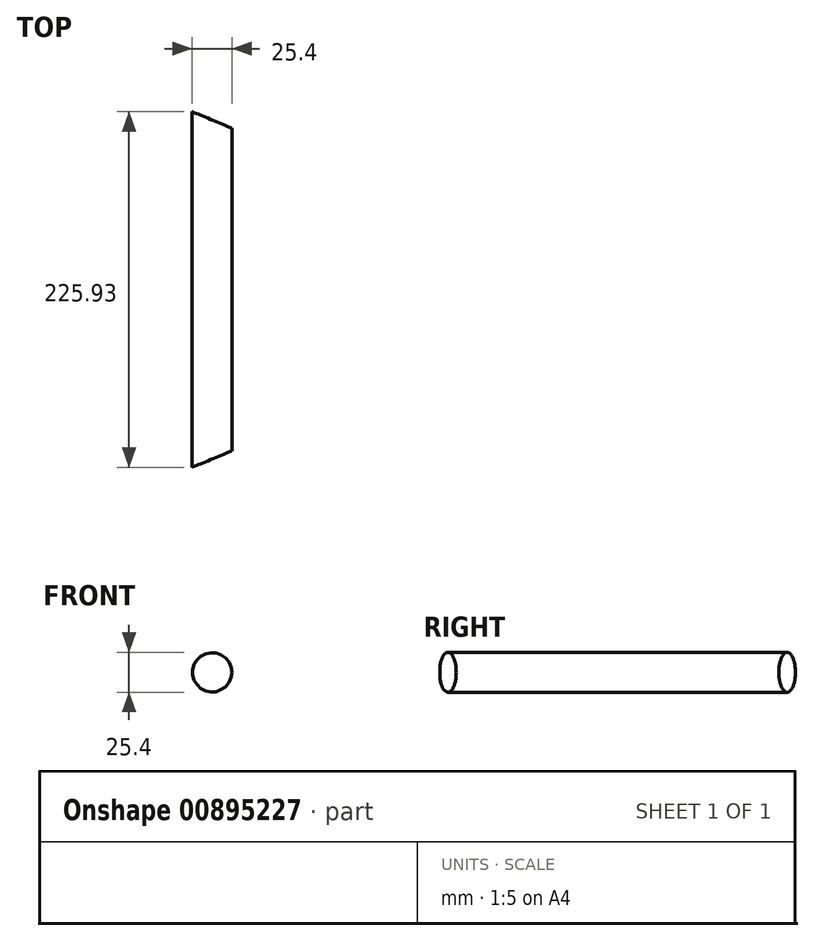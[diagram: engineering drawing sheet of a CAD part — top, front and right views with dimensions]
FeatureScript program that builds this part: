
annotation { "Feature Type Name" : "Feature", "Feature Type Description" : "" }
export const myFeature = defineFeature(function(context is Context, id is Id, definition is map)
    precondition{}
    {
        {
            var Q0;
            Q0=qCreatedBy(makeId("Front.planeOp"),FACE);
            var sketch = newSketch(context, id + "F0", { "sketchPlane" : qUnion([Q0])});
            skCircle(sketch, "E0", {"center": v(0, 0) * mm, "radius": 12.7 * mm});
            skSolve(sketch);
        }
        {
            var Q0;
            Q0=makeQuery(id+"F0.imprint","IMPRINT",FACE,{"disambiguationData":[TD([[makeQuery(id+"F0.imprint","IMPRINT",EDGE,{"derivedFrom":sQuery(id+"F0.wireOp",EDGE,"E0")}),1.0]])]});
            var sketch = newSketch(context, id + "F1", { "sketchPlane" : qUnion([Q0])});
            skSolve(sketch);
        }
        {
            var Q0;
            Q0=qSketchRegion(id+"F1",true);
            var Q1;
            Q1=makeQuery(id+"F1.imprint","IMPRINT",FACE,{"disambiguationData":[TD([[makeQuery(id+"F1.imprint","IMPRINT",EDGE,{"derivedFrom":makeQuery(id+"F0.imprint","IMPRINT",EDGE,{"derivedFrom":sQuery(id+"F0.wireOp",EDGE,"E0")})}),1.0]])]});
            extrude(context, id + "F2", {"entities" : qUnion([Q0, Q1]), "depth" : 225.93 * mm, "offsetDistance" : 25.4 * mm});
        }
        {
            var Q0;
            Q0=makeQuery(id+"F2.opExtrude","CAP_FACE",FACE,{"disambiguationData":[OSD([sQuery(id+"F0.wireOp",EDGE,"E0")])],"isStart":false});
            cPlane(context, id + "F3", {"entities" : qUnion([Q0]), "cplaneType" : CPlaneType.OFFSET, "offset" : 0 * mm, "width" : 152.4 * mm, "height" : 152.4 * mm});
        }
        {
            var Q0;
            Q0=qCreatedBy(id+"F3.planeOp",FACE);
            var sketch = newSketch(context, id + "F4", { "sketchPlane" : qUnion([Q0])});
            skLineSegment(sketch, "E1.bottom", {"start": v(12.7, 12.7) * mm, "end": v(-12.7, 12.7) * mm});
            skLineSegment(sketch, "E1.top", {"start": v(12.7, -12.7) * mm, "end": v(-12.7, -12.7) * mm});
            skLineSegment(sketch, "E1.left", {"start": v(12.7, 12.7) * mm, "end": v(12.7, -12.7) * mm});
            skLineSegment(sketch, "E1.right", {"start": v(-12.7, 12.7) * mm, "end": v(-12.7, -12.7) * mm});
            skPoint(sketch, "E1.middle", {"position": v(0, 0) * mm});
            skSolve(sketch);
        }
        {
            var Q0;
            Q0=sQuery(id+"F4.wireOp",EDGE,"E1.right");
            cPlane(context, id + "F5", {"entities" : qUnion([Q0]), "cplaneType" : CPlaneType.LINE_ANGLE, "offset" : 25.4 * mm, "angle" : 67.5 * degree, "width" : 152.4 * mm, "height" : 152.4 * mm});
        }
        {
            var Q0;
            Q0=qCreatedBy(id+"F5.planeOp",FACE);
            var sketch = newSketch(context, id + "F6", { "sketchPlane" : qUnion([Q0])});
            skLineSegment(sketch, "E2.bottom", {"start": v(61.14, -41.3) * mm, "end": v(175.23, -41.3) * mm});
            skLineSegment(sketch, "E2.top", {"start": v(61.14, 47.2) * mm, "end": v(175.23, 47.2) * mm});
            skLineSegment(sketch, "E2.left", {"start": v(61.14, -41.3) * mm, "end": v(61.14, 47.2) * mm});
            skLineSegment(sketch, "E2.right", {"start": v(175.23, -41.3) * mm, "end": v(175.23, 47.2) * mm});
            skPoint(sketch, "E2.middle", {"position": v(118.19, 2.95) * mm});
            skSolve(sketch);
        }
        {
            var Q0;
            Q0=makeQuery(id+"F6.imprint","IMPRINT",FACE,{"disambiguationData":[TD([[makeQuery(id+"F6.imprint","IMPRINT",EDGE,{"derivedFrom":sQuery(id+"F6.wireOp",EDGE,"E2.bottom")}),1.0]])]});
            extrude(context, id + "F7", {"entities" : qUnion([Q0]), "operationType" : NewBodyOperationType.REMOVE, "oppositeDirection" : true, "depth" : 25.4 * mm, "offsetDistance" : 25.4 * mm});
        }
        {
            var Q0;
            Q0=makeQuery(id+"F0.imprint","IMPRINT",FACE,{"disambiguationData":[TD([[makeQuery(id+"F0.imprint","IMPRINT",EDGE,{"derivedFrom":sQuery(id+"F0.wireOp",EDGE,"E0")}),1.0]])]});
            cPlane(context, id + "F8", {"entities" : qUnion([Q0]), "cplaneType" : CPlaneType.OFFSET, "offset" : 0 * mm, "width" : 152.4 * mm, "height" : 152.4 * mm});
        }
        {
            var Q0;
            Q0=qCreatedBy(id+"F8.planeOp",FACE);
            var sketch = newSketch(context, id + "F9", { "sketchPlane" : qUnion([Q0])});
            skLineSegment(sketch, "E3.bottom", {"start": v(-12.7, -12.7) * mm, "end": v(12.7, -12.7) * mm});
            skLineSegment(sketch, "E3.top", {"start": v(-12.7, 12.7) * mm, "end": v(12.7, 12.7) * mm});
            skLineSegment(sketch, "E3.left", {"start": v(-12.7, -12.7) * mm, "end": v(-12.7, 12.7) * mm});
            skLineSegment(sketch, "E3.right", {"start": v(12.7, -12.7) * mm, "end": v(12.7, 12.7) * mm});
            skPoint(sketch, "E3.middle", {"position": v(0, 0) * mm});
            skSolve(sketch);
        }
        {
            var Q0;
            Q0=sQuery(id+"F9.wireOp",EDGE,"E3.left");
            cPlane(context, id + "F10", {"entities" : qUnion([Q0]), "cplaneType" : CPlaneType.LINE_ANGLE, "offset" : 25.4 * mm, "angle" : 67.5 * degree, "width" : 152.4 * mm, "height" : 152.4 * mm});
        }
        {
            var Q0;
            Q0=qCreatedBy(id+"F10.planeOp",FACE);
            var sketch = newSketch(context, id + "F11", { "sketchPlane" : qUnion([Q0])});
            skLineSegment(sketch, "E4.bottom", {"start": v(72.83, 41.24) * mm, "end": v(-72.83, 41.24) * mm});
            skLineSegment(sketch, "E4.top", {"start": v(72.83, -41.24) * mm, "end": v(-72.83, -41.24) * mm});
            skLineSegment(sketch, "E4.left", {"start": v(72.83, 41.24) * mm, "end": v(72.83, -41.24) * mm});
            skLineSegment(sketch, "E4.right", {"start": v(-72.83, 41.24) * mm, "end": v(-72.83, -41.24) * mm});
            skPoint(sketch, "E4.middle", {"position": v(0, 0) * mm});
            skSolve(sketch);
        }
        {
            var Q0;
            Q0=qSketchRegion(id+"F11",true);
            extrude(context, id + "F12", {"entities" : qUnion([Q0]), "operationType" : NewBodyOperationType.REMOVE, "depth" : 25.4 * mm, "offsetDistance" : 25.4 * mm});
        }
    });
